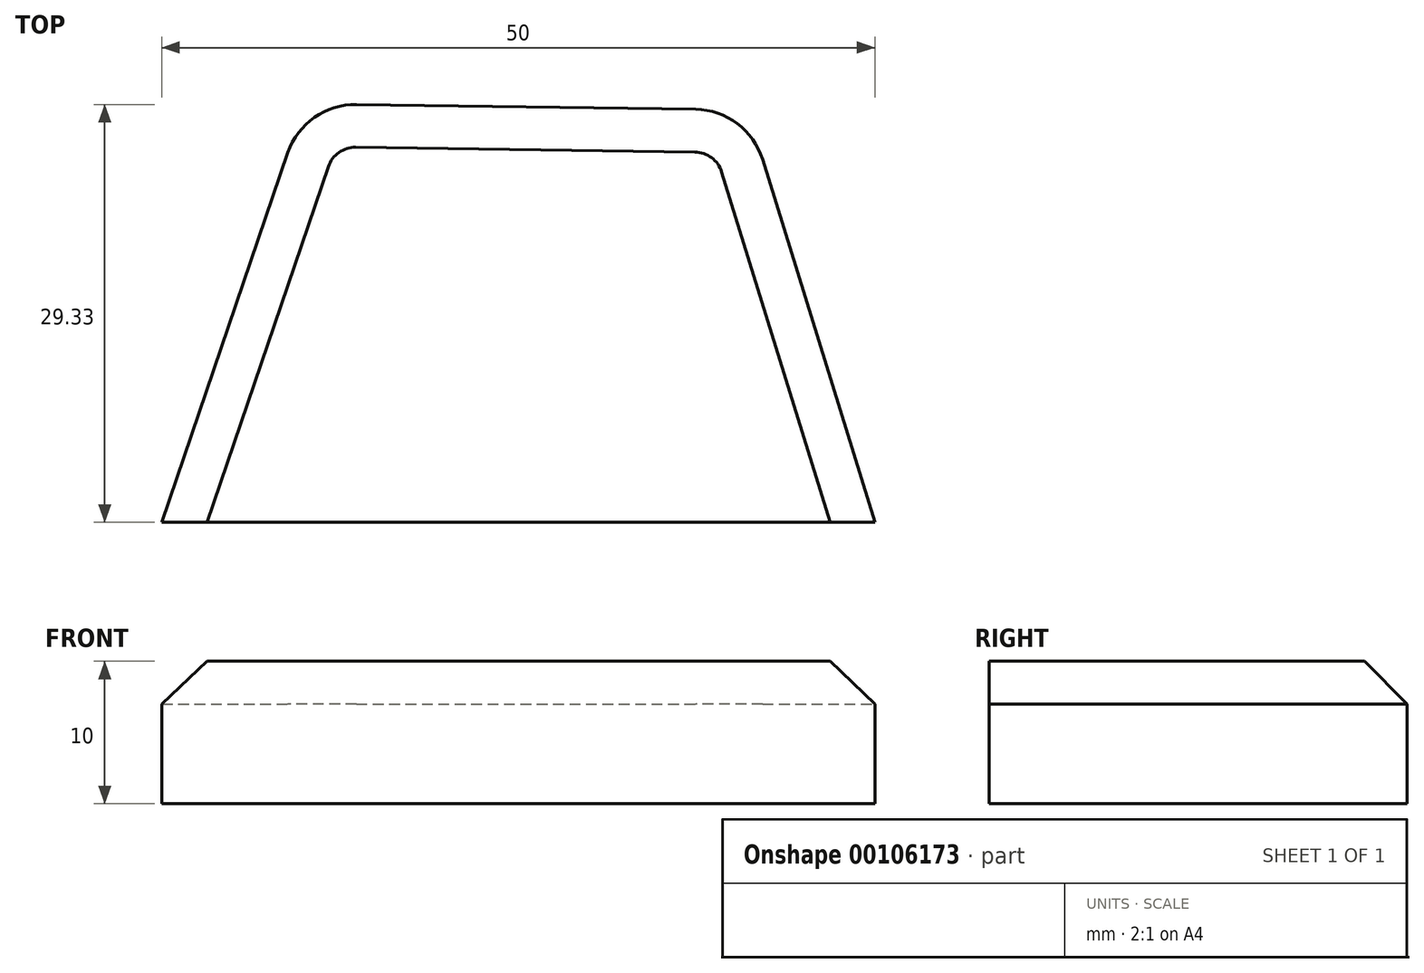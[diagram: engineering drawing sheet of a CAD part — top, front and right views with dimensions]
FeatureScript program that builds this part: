
annotation { "Feature Type Name" : "Feature", "Feature Type Description" : "" }
export const myFeature = defineFeature(function(context is Context, id is Id, definition is map)
    precondition{}
    {
        {
            var Q0;
            Q0=qCreatedBy(makeId("Top.planeOp"),FACE);
            var sketch = newSketch(context, id + "F0", { "sketchPlane" : qUnion([Q0])});
            skArc(sketch, "E0.cCircle", {"start": v(19.89, -7.8) * mm, "mid": v(0, 21.36) * mm, "end": v(-19.89, -7.8) * mm, "construction": true});
            skLineSegment(sketch, "E0.2", {"start": v(-25.23, -7.8) * mm, "end": v(-15.22, 21.58) * mm});
            skLineSegment(sketch, "E0.3", {"start": v(-15.22, 21.58) * mm, "end": v(15.82, 21.14) * mm});
            skLineSegment(sketch, "E0.4", {"start": v(15.82, 21.14) * mm, "end": v(24.77, -7.8) * mm});
            skLineSegment(sketch, "E1", {"start": v(24.77, -7.8) * mm, "end": v(-25.23, -7.8) * mm});
            skSolve(sketch);
        }
        {
            var Q0;
            Q0 = qSketchRegion(id + "F0", true);
            extrude(context, id + "F1", {"entities" : qUnion([Q0]), "depth" : 10 * mm});
        }
        {
            var Q0;
            Q0=makeQuery(id+"F1.opExtrude","SWEPT_EDGE",EDGE,{"disambiguationData":[OSD([sQuery(id+"F0.wireOp",EDGE,"E0.2"),sQuery(id+"F0.wireOp",EDGE,"E0.3")])]});
            var Q1;
            Q1=makeQuery(id+"F1.opExtrude","SWEPT_EDGE",EDGE,{"disambiguationData":[OSD([sQuery(id+"F0.wireOp",EDGE,"E0.3"),sQuery(id+"F0.wireOp",EDGE,"E0.4")])]});
            fillet(context, id + "F2", {"entities" : qUnion([Q0, Q1]), "radius" : 5 * mm, "tangentPropagation" : true, "allowEdgeOverflow" : false});
        }
        {
            var Q0;
            Q0=makeQuery(id+"F1.opExtrude","CAP_EDGE",EDGE,{"disambiguationData":[OSD([sQuery(id+"F0.wireOp",EDGE,"E0.4")])],"isStart":false});
            var Q1;
            {var subQ0=sQuery(id+"F0.wireOp",EDGE,"E0.4");var subQ1=sQuery(id+"F0.wireOp",EDGE,"E0.3");Q1=makeQuery(id+"F2.opFillet","BLEND_EDGE",EDGE,{"blendedFrom":[makeQuery(id+"F1.opExtrude","SWEPT_EDGE",EDGE,{"disambiguationData":[OSD([subQ1,subQ0])]}),makeQuery(id+"F1.opExtrude","CAP_FACE",FACE,{"disambiguationData":[OSD([sQuery(id+"F0.wireOp",EDGE,"E0.2"),subQ1,subQ0,sQuery(id+"F0.wireOp",EDGE,"E1")])],"isStart":false})],"blendedInto":[makeQuery(id+"F1.opExtrude","CAP_FACE",FACE,{"disambiguationData":[OSD([sQuery(id+"F0.wireOp",EDGE,"E0.2"),subQ1,subQ0,sQuery(id+"F0.wireOp",EDGE,"E1")])],"isStart":false})]});}
            var Q2;
            Q2=makeQuery(id+"F1.opExtrude","CAP_EDGE",EDGE,{"disambiguationData":[OSD([sQuery(id+"F0.wireOp",EDGE,"E0.3")])],"isStart":false});
            var Q3;
            {var subQ0=sQuery(id+"F0.wireOp",EDGE,"E0.3");var subQ1=sQuery(id+"F0.wireOp",EDGE,"E0.2");Q3=makeQuery(id+"F2.opFillet","BLEND_EDGE",EDGE,{"blendedFrom":[makeQuery(id+"F1.opExtrude","SWEPT_EDGE",EDGE,{"disambiguationData":[OSD([subQ1,subQ0])]}),makeQuery(id+"F1.opExtrude","CAP_FACE",FACE,{"disambiguationData":[OSD([subQ1,subQ0,sQuery(id+"F0.wireOp",EDGE,"E0.4"),sQuery(id+"F0.wireOp",EDGE,"E1")])],"isStart":false})],"blendedInto":[makeQuery(id+"F1.opExtrude","CAP_FACE",FACE,{"disambiguationData":[OSD([subQ1,subQ0,sQuery(id+"F0.wireOp",EDGE,"E0.4"),sQuery(id+"F0.wireOp",EDGE,"E1")])],"isStart":false})]});}
            var Q4;
            Q4=makeQuery(id+"F1.opExtrude","CAP_EDGE",EDGE,{"disambiguationData":[OSD([sQuery(id+"F0.wireOp",EDGE,"E0.2")])],"isStart":false});
            chamfer(context, id + "F3", {"entities" : qUnion([Q0, Q1, Q2, Q3, Q4]), "width" : 3 * mm, "tangentPropagation" : true});
        }
    });
